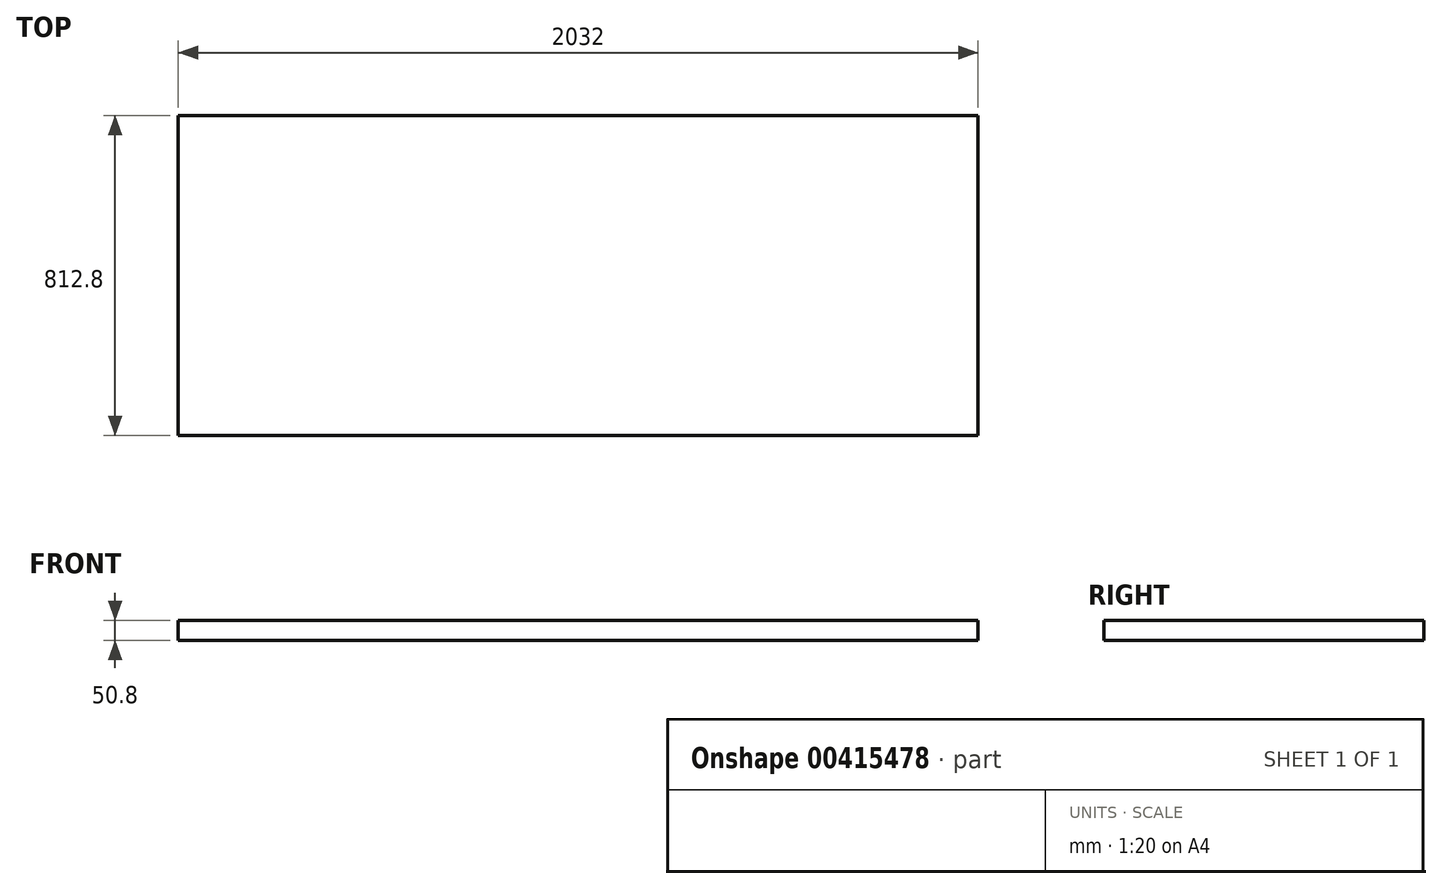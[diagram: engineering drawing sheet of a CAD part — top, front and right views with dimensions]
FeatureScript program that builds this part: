
annotation { "Feature Type Name" : "Feature", "Feature Type Description" : "" }
export const myFeature = defineFeature(function(context is Context, id is Id, definition is map)
    precondition{}
    {
        {
            var Q0;
            Q0=qCreatedBy(makeId("Top.planeOp"),FACE);
            var sketch = newSketch(context, id + "F0", { "sketchPlane" : qUnion([Q0])});
            skLineSegment(sketch, "E0.bottom", {"start": v(-1921.83, 2717.8) * mm, "end": v(110.17, 2717.8) * mm});
            skLineSegment(sketch, "E0.top", {"start": v(-1921.83, 1905) * mm, "end": v(110.17, 1905) * mm});
            skLineSegment(sketch, "E0.left", {"start": v(-1921.83, 2717.8) * mm, "end": v(-1921.83, 1905) * mm});
            skLineSegment(sketch, "E0.right", {"start": v(110.17, 2717.8) * mm, "end": v(110.17, 1905) * mm});
            skPoint(sketch, "E1", {"position": v(-1109.03, 1905) * mm});
            skLineSegment(sketch, "E2.bottom", {"start": v(-1921.83, 1905) * mm, "end": v(-1109.03, 1905) * mm});
            skLineSegment(sketch, "E2.top", {"start": v(-1921.83, -838.2) * mm, "end": v(-1109.03, -838.2) * mm});
            skLineSegment(sketch, "E2.left", {"start": v(-1921.83, 1905) * mm, "end": v(-1921.83, -838.2) * mm});
            skLineSegment(sketch, "E2.right", {"start": v(-1109.03, 1905) * mm, "end": v(-1109.03, -838.2) * mm});
            skCircle(sketch, "E3", {"center": v(-1515.43, -679.45) * mm, "radius": 19.05 * mm});
            skPoint(sketch, "E3.centerSnap0", {"position": v(-1515.43, -838.2) * mm});
            skLineSegment(sketch, "E4.bottom", {"start": v(-1845.63, -609.6) * mm, "end": v(-1185.23, -609.6) * mm});
            skLineSegment(sketch, "E4.top", {"start": v(-1845.63, 0) * mm, "end": v(-1185.23, 0) * mm});
            skLineSegment(sketch, "E4.left", {"start": v(-1845.63, -609.6) * mm, "end": v(-1845.63, 0) * mm});
            skLineSegment(sketch, "E4.right", {"start": v(-1185.23, -609.6) * mm, "end": v(-1185.23, 0) * mm});
            skLineSegment(sketch, "E5.bottom", {"start": v(-1845.63, 762) * mm, "end": v(-1185.23, 762) * mm});
            skLineSegment(sketch, "E5.top", {"start": v(-1845.63, 1524) * mm, "end": v(-1185.23, 1524) * mm});
            skLineSegment(sketch, "E5.left", {"start": v(-1845.63, 762) * mm, "end": v(-1845.63, 1524) * mm});
            skLineSegment(sketch, "E5.right", {"start": v(-1185.23, 762) * mm, "end": v(-1185.23, 1524) * mm});
            skSolve(sketch);
        }
        {
            var Q0;
            Q0=makeQuery(id+"F0.imprint","IMPRINT",FACE,{"disambiguationData":[TD([[makeQuery(id+"F0.imprint","IMPRINT",EDGE,{"derivedFrom":sQuery(id+"F0.wireOp",EDGE,"E2.bottom")}),-1.0]])]});
            var Q1;
            Q1=makeQuery(id+"F0.imprint","IMPRINT",FACE,{"disambiguationData":[TD([[makeQuery(id+"F0.imprint","IMPRINT",EDGE,{"derivedFrom":sQuery(id+"F0.wireOp",EDGE,"E0.bottom")}),-1.0]])]});
            extrude(context, id + "F1", {"entities" : qUnion([Q0, Q1]), "depth" : 50.8 * mm});
        }
    });
